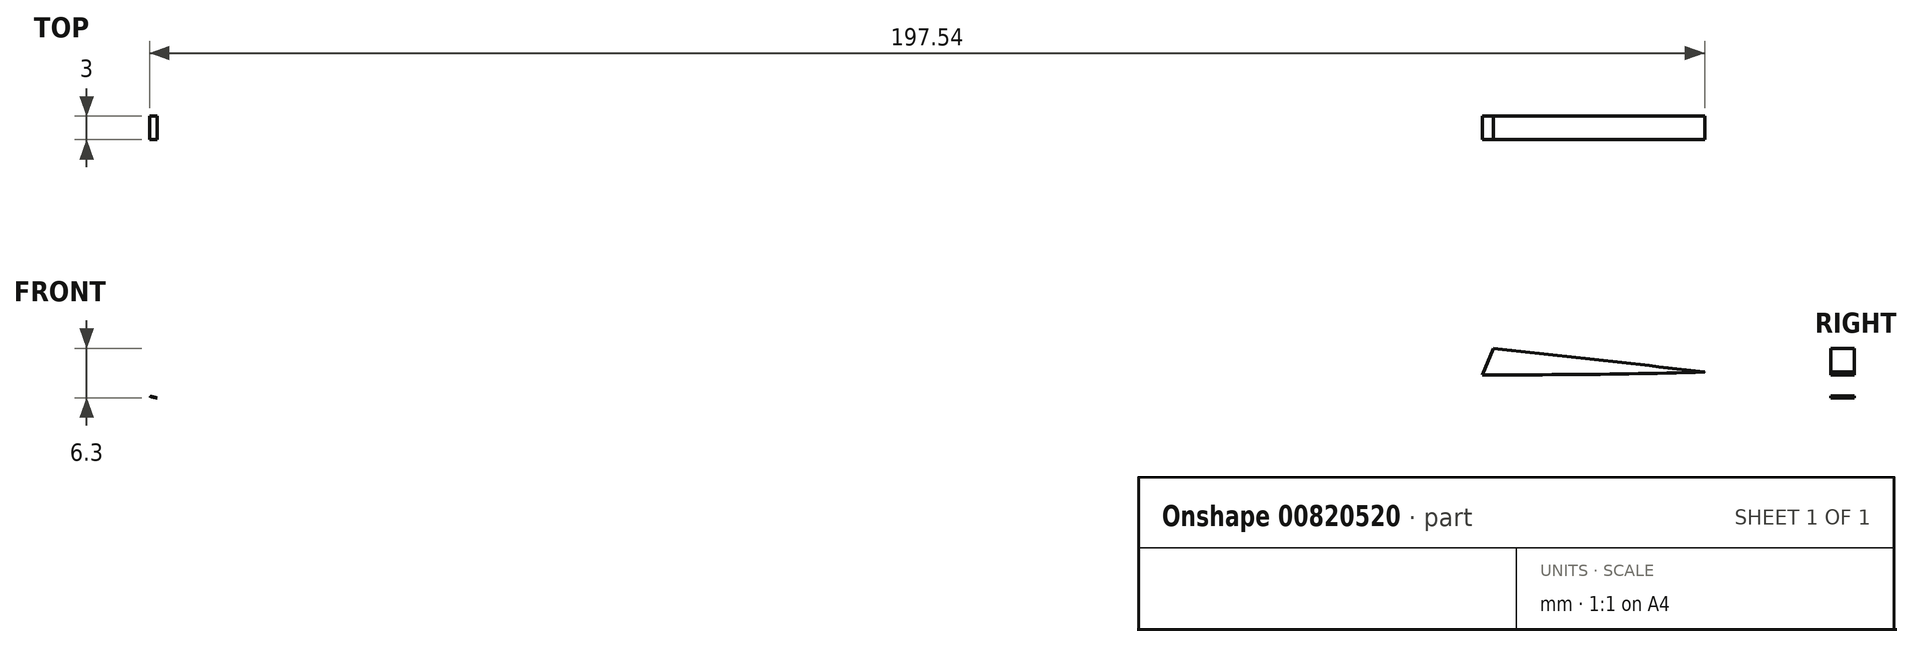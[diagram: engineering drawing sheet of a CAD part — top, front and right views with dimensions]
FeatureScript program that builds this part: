
annotation { "Feature Type Name" : "Feature", "Feature Type Description" : "" }
export const myFeature = defineFeature(function(context is Context, id is Id, definition is map)
    precondition{}
    {
        {
            var Q0;
            Q0=qCreatedBy(makeId("Front.planeOp"),FACE);
            var sketch = newSketch(context, id + "F0", { "sketchPlane" : qUnion([Q0])});
            skPoint(sketch, "E0.middle", {"position": v(0, 0) * mm});
            skLineSegment(sketch, "E1", {"start": v(-99.95, -4.05) * mm, "end": v(-99.64, -4.05) * mm});
            skFitSpline(sketch, "E2", {"points": [v(-96.98, -0.81) * mm, v(-45.24, 7.5) * mm, v(100, -4.05) * mm], "startDerivative": vector(97.58, 47.67) * mm, "endDerivative": vector(275.05, -31.29) * mm});
            skFitSpline(sketch, "E3", {"points": [v(-96.54, -7.34) * mm, v(-44.56, -9.6) * mm, v(41.7, -4.97) * mm, v(100, -4.05) * mm], "startDerivative": vector(159.07, -20.98) * mm, "endDerivative": vector(169.88, 6) * mm});
            skFitSpline(sketch, "E4", {"points": [v(-96.54, -7.34) * mm, v(-101.41, -5) * mm, v(-96.98, -0.81) * mm], "startDerivative": vector(-18.7, 3.9) * mm, "endDerivative": vector(17.62, 9.13) * mm});
            skArc(sketch, "E5.trimOffspring", {"start": v(-97.54, -7.12) * mm, "mid": v(-97.05, -7.27) * mm, "end": v(-96.54, -7.34) * mm});
            skFitSpline(sketch, "E6", {"points": [v(-96.34, -1.64) * mm, v(-45.34, 6.27) * mm, v(86.1, -3.38) * mm], "startDerivative": vector(82.57, 38.4) * mm, "endDerivative": vector(239.73, -24.74) * mm});
            skFitSpline(sketch, "E7", {"points": [v(-97.38, -6.05) * mm, v(-44.49, -7.96) * mm, v(41.39, -3.9) * mm, v(86.1, -3.38) * mm], "startDerivative": vector(144.05, -26.77) * mm, "endDerivative": vector(139.27, -2.3) * mm});
            skFitSpline(sketch, "E8", {"points": [v(-97.38, -6.05) * mm, v(-99.95, -4.56) * mm, v(-96.34, -1.64) * mm], "startDerivative": vector(-8.62, 1.03) * mm, "endDerivative": vector(10.24, 4.38) * mm});
            skLineSegment(sketch, "E9", {"start": v(73.15, -1.04) * mm, "end": v(71.8, -4.45) * mm});
            skSolve(sketch);
        }
        {
            var Q0;
            Q0=qCreatedBy(makeId("Front.planeOp"),FACE);
            var sketch = newSketch(context, id + "F1", { "sketchPlane" : qUnion([Q0])});
            skLineSegment(sketch, "E10", {"start": v(-109.84, -5.04) * mm, "end": v(108.45, -3.99) * mm});
            skCircle(sketch, "E11", {"center": v(-49.54, -1.37) * mm, "radius": 4 * mm});
            skCircle(sketch, "E12", {"center": v(33.78, -1.03) * mm, "radius": 2.5 * mm});
            skSolve(sketch);
        }
        {
            var Q0;
            {var subQ1=sQuery(id+"F0.wireOp",EDGE,"E2");Q0=makeQuery(id+"F0.imprint","IMPRINT",FACE,{"disambiguationData":[TD([[makeQuery(id+"F0.imprint","IMPRINT",EDGE,{"derivedFrom":subQ1}),-1.0]])]});}
            var Q1;
            {var subQ1=sQuery(id+"F0.wireOp",EDGE,"E6");Q1=makeQuery(id+"F0.imprint","IMPRINT",FACE,{"disambiguationData":[TD([[makeQuery(id+"F0.imprint","IMPRINT",EDGE,{"derivedFrom":subQ1}),-1.0]])]});}
            var Q2;
            Q2=makeQuery(id+"F1.imprint","IMPRINT",FACE,{"disambiguationData":[TD([[makeQuery(id+"F1.imprint","IMPRINT",EDGE,{"derivedFrom":sQuery(id+"F1.wireOp",EDGE,"E12")}),1.0]])]});
            var Q3;
            {var subQ0=sQuery(id+"F1.wireOp",EDGE,"E11");var subQ1=sQuery(id+"F1.wireOp",EDGE,"E10");var subQ2=makeQuery(id+"F1.imprint","INTERSECT",VERTEX,{"disambiguationData":[OD(0.0)],"derivedFrom":[subQ1,subQ0]});Q3=makeQuery(id+"F1.imprint","IMPRINT",FACE,{"disambiguationData":[TD([[makeQuery(id+"F1.imprint","IMPRINT",EDGE,{"disambiguationData":[TD([[subQ2,-1.0]])],"derivedFrom":subQ1}),1.0]])]});}
            var Q4;
            {var subQ0=sQuery(id+"F1.wireOp",EDGE,"E11");var subQ1=sQuery(id+"F1.wireOp",EDGE,"E10");var subQ2=makeQuery(id+"F1.imprint","INTERSECT",VERTEX,{"disambiguationData":[OD(0.0)],"derivedFrom":[subQ1,subQ0]});Q4=makeQuery(id+"F1.imprint","IMPRINT",FACE,{"disambiguationData":[TD([[makeQuery(id+"F1.imprint","IMPRINT",EDGE,{"disambiguationData":[TD([[subQ2,-1.0]])],"derivedFrom":subQ1}),-1.0]])]});}
            var Q5;
            {var subQ0=sQuery(id+"F0.wireOp",EDGE,"E5.trimOffspring");Q5=makeQuery(id+"F0.imprint","IMPRINT",FACE,{"disambiguationData":[TD([[makeQuery(id+"F0.imprint","IMPRINT",EDGE,{"derivedFrom":subQ0}),1.0]])]});}
            extrude(context, id + "F2", {"entities" : qUnion([Q0, Q1, Q2, Q3, Q4, Q5]), "depth" : 3 * mm, "offsetDistance" : 25 * mm});
        }
        {
            var Q0;
            Q0=makeQuery(id+"F2.opExtrude","CAP_FACE",FACE,{"disambiguationData":[OSD([sQuery(id+"F1.wireOp",EDGE,"E11")])],"isStart":false});
            extrude(context, id + "F3", {"entities" : qUnion([Q0]), "operationType" : NewBodyOperationType.REMOVE, "oppositeDirection" : true, "depth" : 3 * mm, "offsetDistance" : 25 * mm});
        }
        {
            var Q0;
            Q0=makeQuery(id+"F2.opExtrude","CAP_FACE",FACE,{"disambiguationData":[OSD([sQuery(id+"F1.wireOp",EDGE,"E12")])],"isStart":false});
            extrude(context, id + "F4", {"entities" : qUnion([Q0]), "operationType" : NewBodyOperationType.REMOVE, "oppositeDirection" : true, "depth" : 3 * mm, "offsetDistance" : 25 * mm});
        }
    });
